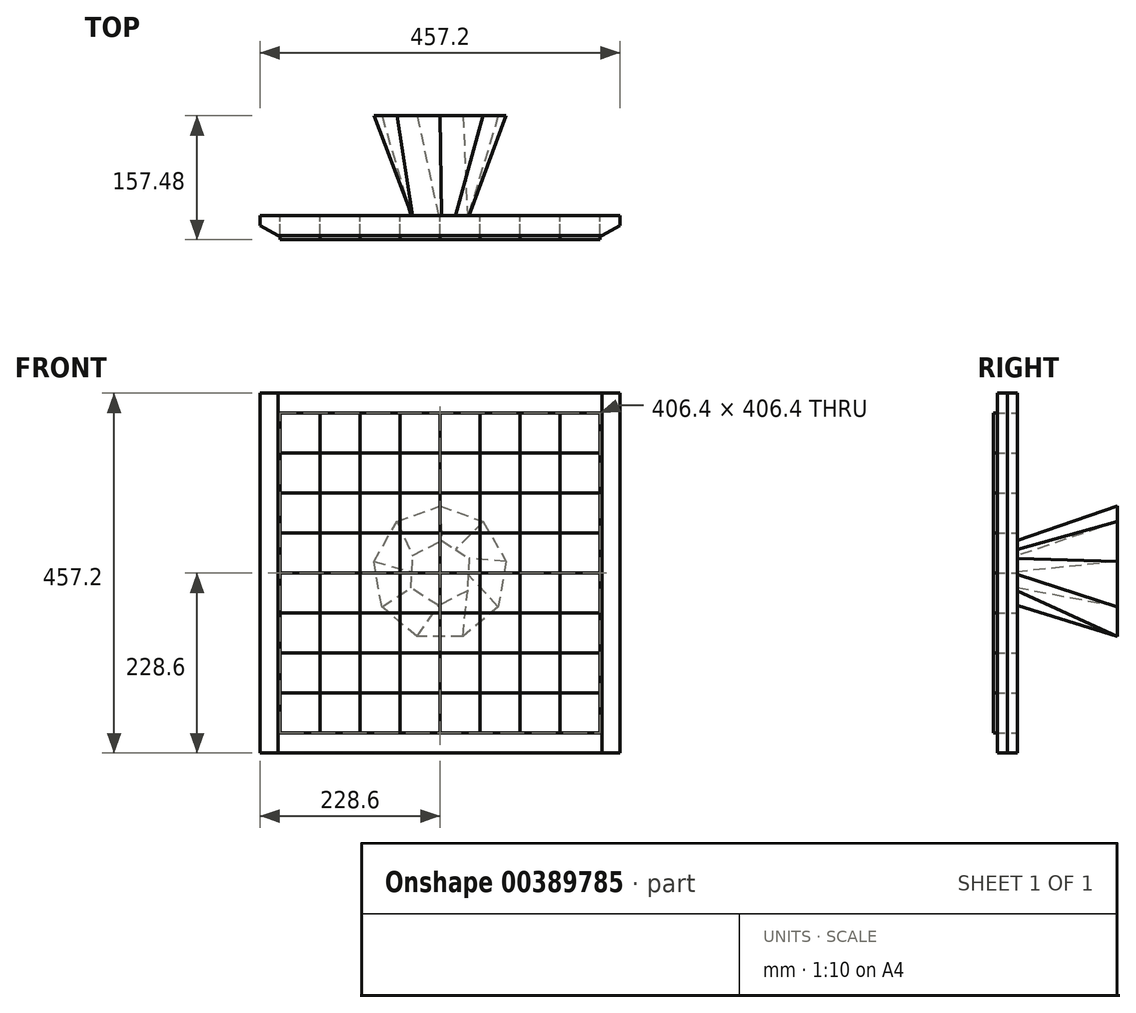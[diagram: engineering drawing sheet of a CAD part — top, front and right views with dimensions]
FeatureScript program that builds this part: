
annotation { "Feature Type Name" : "Feature", "Feature Type Description" : "" }
export const myFeature = defineFeature(function(context is Context, id is Id, definition is map)
    precondition{}
    {
        {
            var Q0;
            Q0=qCreatedBy(makeId("Front.planeOp"),FACE);
            var sketch = newSketch(context, id + "F0", { "sketchPlane" : qUnion([Q0])});
            skLineSegment(sketch, "E0.left", {"start": v(-203.2, 203.2) * mm, "end": v(-203.2, 0) * mm});
            skLineSegment(sketch, "E0.right", {"start": v(203.2, 203.2) * mm, "end": v(203.2, 0) * mm});
            skPoint(sketch, "E0.middle", {"position": v(0, 0) * mm});
            skLineSegment(sketch, "E1", {"start": v(-203.2, 203.2) * mm, "end": v(0, 203.2) * mm});
            skLineSegment(sketch, "E2", {"start": v(0, -203.2) * mm, "end": v(-203.2, -203.2) * mm});
            skLineSegment(sketch, "E3", {"start": v(0, 203.2) * mm, "end": v(0, -203.2) * mm});
            skLineSegment(sketch, "E4", {"start": v(101.6, 203.2) * mm, "end": v(101.6, -203.2) * mm});
            skLineSegment(sketch, "E5", {"start": v(203.2, -203.2) * mm, "end": v(101.6, -203.2) * mm});
            skLineSegment(sketch, "E6", {"start": v(101.6, -203.2) * mm, "end": v(0, -203.2) * mm});
            skLineSegment(sketch, "E7", {"start": v(203.2, 203.2) * mm, "end": v(101.6, 203.2) * mm});
            skLineSegment(sketch, "E8", {"start": v(101.6, 203.2) * mm, "end": v(0, 203.2) * mm});
            skLineSegment(sketch, "E9", {"start": v(50.8, 203.2) * mm, "end": v(50.8, -203.2) * mm});
            skLineSegment(sketch, "E10", {"start": v(152.4, -203.2) * mm, "end": v(152.4, 203.2) * mm});
            skLineSegment(sketch, "E11.MirrorCS", {"start": v(-152.4, -203.2) * mm, "end": v(-152.4, 203.2) * mm});
            skLineSegment(sketch, "E12.MirrorCS", {"start": v(-50.8, 203.2) * mm, "end": v(-50.8, -203.2) * mm});
            skLineSegment(sketch, "E13.MirrorCS", {"start": v(-101.6, 203.2) * mm, "end": v(-101.6, -203.2) * mm});
            skLineSegment(sketch, "E14", {"start": v(203.2, 0) * mm, "end": v(-203.2, 0) * mm});
            skLineSegment(sketch, "E15", {"start": v(203.2, -101.6) * mm, "end": v(-203.2, -101.6) * mm});
            skLineSegment(sketch, "E16", {"start": v(203.2, -203.2) * mm, "end": v(203.2, -101.6) * mm});
            skLineSegment(sketch, "E17", {"start": v(203.2, -101.6) * mm, "end": v(203.2, 0) * mm});
            skLineSegment(sketch, "E18", {"start": v(-203.2, -203.2) * mm, "end": v(-203.2, -101.6) * mm});
            skLineSegment(sketch, "E19", {"start": v(-203.2, -101.6) * mm, "end": v(-203.2, 0) * mm});
            skLineSegment(sketch, "E20", {"start": v(-203.2, -50.8) * mm, "end": v(203.2, -50.8) * mm});
            skLineSegment(sketch, "E21", {"start": v(-203.2, -152.4) * mm, "end": v(203.2, -152.4) * mm});
            skLineSegment(sketch, "E22.MirrorCS", {"start": v(-203.2, 50.8) * mm, "end": v(203.2, 50.8) * mm});
            skLineSegment(sketch, "E23.MirrorCS", {"start": v(203.2, 101.6) * mm, "end": v(-203.2, 101.6) * mm});
            skLineSegment(sketch, "E24.MirrorCS", {"start": v(-203.2, 152.4) * mm, "end": v(203.2, 152.4) * mm});
            skLineSegment(sketch, "E25.0", {"start": v(-228.6, 228.6) * mm, "end": v(-228.6, 0) * mm});
            skLineSegment(sketch, "E25.1", {"start": v(228.6, -101.6) * mm, "end": v(228.6, 0) * mm});
            skLineSegment(sketch, "E25.2", {"start": v(228.6, 228.6) * mm, "end": v(228.6, 0) * mm});
            skLineSegment(sketch, "E25.3", {"start": v(228.6, 228.6) * mm, "end": v(101.6, 228.6) * mm});
            skLineSegment(sketch, "E25.4", {"start": v(101.6, 228.6) * mm, "end": v(0, 228.6) * mm});
            skLineSegment(sketch, "E25.5", {"start": v(228.6, -228.6) * mm, "end": v(228.6, -101.6) * mm});
            skLineSegment(sketch, "E25.6", {"start": v(-228.6, 228.6) * mm, "end": v(0, 228.6) * mm});
            skLineSegment(sketch, "E25.7", {"start": v(228.6, -228.6) * mm, "end": v(101.6, -228.6) * mm});
            skLineSegment(sketch, "E25.8", {"start": v(101.6, -228.6) * mm, "end": v(0, -228.6) * mm});
            skLineSegment(sketch, "E25.9", {"start": v(0, -228.6) * mm, "end": v(-228.6, -228.6) * mm});
            skLineSegment(sketch, "E25.10", {"start": v(-228.6, -228.6) * mm, "end": v(-228.6, -101.6) * mm});
            skLineSegment(sketch, "E25.11", {"start": v(-228.6, -101.6) * mm, "end": v(-228.6, 0) * mm});
            skSolve(sketch);
        }
        {
            var Q0;
            Q0=makeQuery(id+"F0.imprint","IMPRINT",FACE,{"disambiguationData":[TD([[makeQuery(id+"F0.imprint","IMPRINT",EDGE,{"derivedFrom":sQuery(id+"F0.wireOp",EDGE,"E25.0")}),1.0]])]});
            extrude(context, id + "F1", {"entities" : qUnion([Q0]), "depth" : 25.4 * mm});
        }
        {
            var Q0;
            {var subQ0=sQuery(id+"F0.wireOp",EDGE,"E1");var subQ1=sQuery(id+"F0.wireOp",EDGE,"E0.left");var subQ2=makeQuery(id+"F0.imprint","INTERSECT",VERTEX,{"derivedFrom":[subQ1,subQ0]});Q0=makeQuery(id+"F0.imprint","IMPRINT",FACE,{"disambiguationData":[TD([[makeQuery(id+"F0.imprint","IMPRINT",EDGE,{"disambiguationData":[TD([[subQ2,-1.0]])],"derivedFrom":subQ1}),1.0]])]});}
            var Q1;
            {var subQ0=sQuery(id+"F0.wireOp",EDGE,"E13.MirrorCS");var subQ1=sQuery(id+"F0.wireOp",EDGE,"E1");var subQ2=makeQuery(id+"F0.imprint","INTERSECT",VERTEX,{"derivedFrom":[subQ1,subQ0]});Q1=makeQuery(id+"F0.imprint","IMPRINT",FACE,{"disambiguationData":[TD([[makeQuery(id+"F0.imprint","IMPRINT",EDGE,{"disambiguationData":[TD([[subQ2,-1.0]])],"derivedFrom":subQ1}),-1.0]])]});}
            var Q2;
            {var subQ0=sQuery(id+"F0.wireOp",EDGE,"E8");var subQ5=sQuery(id+"F0.wireOp",EDGE,"E9");var subQ6=makeQuery(id+"F0.imprint","INTERSECT",VERTEX,{"derivedFrom":[subQ0,subQ5]});Q2=makeQuery(id+"F0.imprint","IMPRINT",FACE,{"disambiguationData":[TD([[makeQuery(id+"F0.imprint","IMPRINT",EDGE,{"disambiguationData":[TD([[subQ6,-1.0]])],"derivedFrom":subQ5}),-1.0]])]});}
            var Q3;
            {var subQ0=sQuery(id+"F0.wireOp",EDGE,"E7");var subQ5=sQuery(id+"F0.wireOp",EDGE,"E10");var subQ6=makeQuery(id+"F0.imprint","INTERSECT",VERTEX,{"derivedFrom":[subQ0,subQ5]});Q3=makeQuery(id+"F0.imprint","IMPRINT",FACE,{"disambiguationData":[TD([[makeQuery(id+"F0.imprint","IMPRINT",EDGE,{"disambiguationData":[TD([[subQ6,1.0]])],"derivedFrom":subQ5}),1.0]])]});}
            var Q4;
            {var subQ0=sQuery(id+"F0.wireOp",EDGE,"E23.MirrorCS");var subQ1=sQuery(id+"F0.wireOp",EDGE,"E0.right");var subQ2=makeQuery(id+"F0.imprint","INTERSECT",VERTEX,{"derivedFrom":[subQ1,subQ0]});Q4=makeQuery(id+"F0.imprint","IMPRINT",FACE,{"disambiguationData":[TD([[makeQuery(id+"F0.imprint","IMPRINT",EDGE,{"disambiguationData":[TD([[subQ2,1.0]])],"derivedFrom":subQ1}),-1.0]])]});}
            var Q5;
            {var subQ0=sQuery(id+"F0.wireOp",EDGE,"E24.MirrorCS");var subQ1=sQuery(id+"F0.wireOp",EDGE,"E4");var subQ2=makeQuery(id+"F0.imprint","INTERSECT",VERTEX,{"derivedFrom":[subQ1,subQ0]});Q5=makeQuery(id+"F0.imprint","IMPRINT",FACE,{"disambiguationData":[TD([[makeQuery(id+"F0.imprint","IMPRINT",EDGE,{"disambiguationData":[TD([[subQ2,-1.0]])],"derivedFrom":subQ1}),-1.0]])]});}
            var Q6;
            {var subQ0=sQuery(id+"F0.wireOp",EDGE,"E24.MirrorCS");var subQ1=sQuery(id+"F0.wireOp",EDGE,"E3");var subQ2=makeQuery(id+"F0.imprint","INTERSECT",VERTEX,{"derivedFrom":[subQ1,subQ0]});Q6=makeQuery(id+"F0.imprint","IMPRINT",FACE,{"disambiguationData":[TD([[makeQuery(id+"F0.imprint","IMPRINT",EDGE,{"disambiguationData":[TD([[subQ2,-1.0]])],"derivedFrom":subQ1}),-1.0]])]});}
            var Q7;
            {var subQ0=sQuery(id+"F0.wireOp",EDGE,"E23.MirrorCS");var subQ1=sQuery(id+"F0.wireOp",EDGE,"E11.MirrorCS");var subQ2=makeQuery(id+"F0.imprint","INTERSECT",VERTEX,{"derivedFrom":[subQ1,subQ0]});Q7=makeQuery(id+"F0.imprint","IMPRINT",FACE,{"disambiguationData":[TD([[makeQuery(id+"F0.imprint","IMPRINT",EDGE,{"disambiguationData":[TD([[subQ2,-1.0]])],"derivedFrom":subQ1}),-1.0]])]});}
            var Q8;
            {var subQ0=sQuery(id+"F0.wireOp",EDGE,"E22.MirrorCS");var subQ1=sQuery(id+"F0.wireOp",EDGE,"E0.left");var subQ2=makeQuery(id+"F0.imprint","INTERSECT",VERTEX,{"derivedFrom":[subQ1,subQ0]});Q8=makeQuery(id+"F0.imprint","IMPRINT",FACE,{"disambiguationData":[TD([[makeQuery(id+"F0.imprint","IMPRINT",EDGE,{"disambiguationData":[TD([[subQ2,1.0]])],"derivedFrom":subQ1}),1.0]])]});}
            var Q9;
            {var subQ0=sQuery(id+"F0.wireOp",EDGE,"E23.MirrorCS");var subQ1=sQuery(id+"F0.wireOp",EDGE,"E13.MirrorCS");var subQ2=makeQuery(id+"F0.imprint","INTERSECT",VERTEX,{"derivedFrom":[subQ1,subQ0]});Q9=makeQuery(id+"F0.imprint","IMPRINT",FACE,{"disambiguationData":[TD([[makeQuery(id+"F0.imprint","IMPRINT",EDGE,{"disambiguationData":[TD([[subQ2,-1.0]])],"derivedFrom":subQ1}),1.0]])]});}
            var Q10;
            {var subQ0=sQuery(id+"F0.wireOp",EDGE,"E23.MirrorCS");var subQ1=sQuery(id+"F0.wireOp",EDGE,"E3");var subQ2=makeQuery(id+"F0.imprint","INTERSECT",VERTEX,{"derivedFrom":[subQ1,subQ0]});Q10=makeQuery(id+"F0.imprint","IMPRINT",FACE,{"disambiguationData":[TD([[makeQuery(id+"F0.imprint","IMPRINT",EDGE,{"disambiguationData":[TD([[subQ2,-1.0]])],"derivedFrom":subQ1}),1.0]])]});}
            var Q11;
            {var subQ0=sQuery(id+"F0.wireOp",EDGE,"E23.MirrorCS");var subQ1=sQuery(id+"F0.wireOp",EDGE,"E4");var subQ2=makeQuery(id+"F0.imprint","INTERSECT",VERTEX,{"derivedFrom":[subQ1,subQ0]});Q11=makeQuery(id+"F0.imprint","IMPRINT",FACE,{"disambiguationData":[TD([[makeQuery(id+"F0.imprint","IMPRINT",EDGE,{"disambiguationData":[TD([[subQ2,-1.0]])],"derivedFrom":subQ1}),1.0]])]});}
            var Q12;
            {var subQ0=sQuery(id+"F0.wireOp",EDGE,"E14");var subQ5=sQuery(id+"F0.wireOp",EDGE,"E10");var subQ6=makeQuery(id+"F0.imprint","INTERSECT",VERTEX,{"derivedFrom":[subQ5,subQ0]});Q12=makeQuery(id+"F0.imprint","IMPRINT",FACE,{"disambiguationData":[TD([[makeQuery(id+"F0.imprint","IMPRINT",EDGE,{"disambiguationData":[TD([[subQ6,-1.0]])],"derivedFrom":subQ5}),-1.0]])]});}
            var Q13;
            {var subQ0=sQuery(id+"F0.wireOp",EDGE,"E22.MirrorCS");var subQ1=sQuery(id+"F0.wireOp",EDGE,"E4");var subQ2=makeQuery(id+"F0.imprint","INTERSECT",VERTEX,{"derivedFrom":[subQ1,subQ0]});Q13=makeQuery(id+"F0.imprint","IMPRINT",FACE,{"disambiguationData":[TD([[makeQuery(id+"F0.imprint","IMPRINT",EDGE,{"disambiguationData":[TD([[subQ2,-1.0]])],"derivedFrom":subQ1}),-1.0]])]});}
            var Q14;
            {var subQ0=sQuery(id+"F0.wireOp",EDGE,"E22.MirrorCS");var subQ1=sQuery(id+"F0.wireOp",EDGE,"E3");var subQ2=makeQuery(id+"F0.imprint","INTERSECT",VERTEX,{"derivedFrom":[subQ1,subQ0]});Q14=makeQuery(id+"F0.imprint","IMPRINT",FACE,{"disambiguationData":[TD([[makeQuery(id+"F0.imprint","IMPRINT",EDGE,{"disambiguationData":[TD([[subQ2,-1.0]])],"derivedFrom":subQ1}),-1.0]])]});}
            var Q15;
            {var subQ0=sQuery(id+"F0.wireOp",EDGE,"E14");var subQ1=sQuery(id+"F0.wireOp",EDGE,"E11.MirrorCS");var subQ2=makeQuery(id+"F0.imprint","INTERSECT",VERTEX,{"derivedFrom":[subQ1,subQ0]});Q15=makeQuery(id+"F0.imprint","IMPRINT",FACE,{"disambiguationData":[TD([[makeQuery(id+"F0.imprint","IMPRINT",EDGE,{"disambiguationData":[TD([[subQ2,-1.0]])],"derivedFrom":subQ1}),-1.0]])]});}
            var Q16;
            {var subQ0=sQuery(id+"F0.wireOp",EDGE,"E20");var subQ1=sQuery(id+"F0.wireOp",EDGE,"E11.MirrorCS");var subQ2=makeQuery(id+"F0.imprint","INTERSECT",VERTEX,{"derivedFrom":[subQ1,subQ0]});Q16=makeQuery(id+"F0.imprint","IMPRINT",FACE,{"disambiguationData":[TD([[makeQuery(id+"F0.imprint","IMPRINT",EDGE,{"disambiguationData":[TD([[subQ2,-1.0]])],"derivedFrom":subQ1}),1.0]])]});}
            var Q17;
            {var subQ0=sQuery(id+"F0.wireOp",EDGE,"E14");var subQ1=sQuery(id+"F0.wireOp",EDGE,"E13.MirrorCS");var subQ2=makeQuery(id+"F0.imprint","INTERSECT",VERTEX,{"derivedFrom":[subQ1,subQ0]});Q17=makeQuery(id+"F0.imprint","IMPRINT",FACE,{"disambiguationData":[TD([[makeQuery(id+"F0.imprint","IMPRINT",EDGE,{"disambiguationData":[TD([[subQ2,-1.0]])],"derivedFrom":subQ1}),1.0]])]});}
            var Q18;
            {var subQ0=sQuery(id+"F0.wireOp",EDGE,"E14");var subQ1=sQuery(id+"F0.wireOp",EDGE,"E3");var subQ2=makeQuery(id+"F0.imprint","INTERSECT",VERTEX,{"derivedFrom":[subQ1,subQ0]});Q18=makeQuery(id+"F0.imprint","IMPRINT",FACE,{"disambiguationData":[TD([[makeQuery(id+"F0.imprint","IMPRINT",EDGE,{"disambiguationData":[TD([[subQ2,-1.0]])],"derivedFrom":subQ1}),1.0]])]});}
            var Q19;
            {var subQ0=sQuery(id+"F0.wireOp",EDGE,"E14");var subQ1=sQuery(id+"F0.wireOp",EDGE,"E4");var subQ2=makeQuery(id+"F0.imprint","INTERSECT",VERTEX,{"derivedFrom":[subQ1,subQ0]});Q19=makeQuery(id+"F0.imprint","IMPRINT",FACE,{"disambiguationData":[TD([[makeQuery(id+"F0.imprint","IMPRINT",EDGE,{"disambiguationData":[TD([[subQ2,-1.0]])],"derivedFrom":subQ1}),1.0]])]});}
            var Q20;
            {var subQ0=sQuery(id+"F0.wireOp",EDGE,"E15");var subQ1=sQuery(id+"F0.wireOp",EDGE,"E10");var subQ2=makeQuery(id+"F0.imprint","INTERSECT",VERTEX,{"derivedFrom":[subQ1,subQ0]});Q20=makeQuery(id+"F0.imprint","IMPRINT",FACE,{"disambiguationData":[TD([[makeQuery(id+"F0.imprint","IMPRINT",EDGE,{"disambiguationData":[TD([[subQ2,-1.0]])],"derivedFrom":subQ1}),-1.0]])]});}
            var Q21;
            {var subQ0=sQuery(id+"F0.wireOp",EDGE,"E20");var subQ1=sQuery(id+"F0.wireOp",EDGE,"E4");var subQ2=makeQuery(id+"F0.imprint","INTERSECT",VERTEX,{"derivedFrom":[subQ1,subQ0]});Q21=makeQuery(id+"F0.imprint","IMPRINT",FACE,{"disambiguationData":[TD([[makeQuery(id+"F0.imprint","IMPRINT",EDGE,{"disambiguationData":[TD([[subQ2,-1.0]])],"derivedFrom":subQ1}),-1.0]])]});}
            var Q22;
            {var subQ0=sQuery(id+"F0.wireOp",EDGE,"E20");var subQ1=sQuery(id+"F0.wireOp",EDGE,"E3");var subQ2=makeQuery(id+"F0.imprint","INTERSECT",VERTEX,{"derivedFrom":[subQ1,subQ0]});Q22=makeQuery(id+"F0.imprint","IMPRINT",FACE,{"disambiguationData":[TD([[makeQuery(id+"F0.imprint","IMPRINT",EDGE,{"disambiguationData":[TD([[subQ2,-1.0]])],"derivedFrom":subQ1}),-1.0]])]});}
            var Q23;
            {var subQ0=sQuery(id+"F0.wireOp",EDGE,"E15");var subQ1=sQuery(id+"F0.wireOp",EDGE,"E11.MirrorCS");var subQ2=makeQuery(id+"F0.imprint","INTERSECT",VERTEX,{"derivedFrom":[subQ1,subQ0]});Q23=makeQuery(id+"F0.imprint","IMPRINT",FACE,{"disambiguationData":[TD([[makeQuery(id+"F0.imprint","IMPRINT",EDGE,{"disambiguationData":[TD([[subQ2,-1.0]])],"derivedFrom":subQ1}),-1.0]])]});}
            var Q24;
            {var subQ0=sQuery(id+"F0.wireOp",EDGE,"E21");var subQ1=sQuery(id+"F0.wireOp",EDGE,"E11.MirrorCS");var subQ2=makeQuery(id+"F0.imprint","INTERSECT",VERTEX,{"derivedFrom":[subQ1,subQ0]});Q24=makeQuery(id+"F0.imprint","IMPRINT",FACE,{"disambiguationData":[TD([[makeQuery(id+"F0.imprint","IMPRINT",EDGE,{"disambiguationData":[TD([[subQ2,-1.0]])],"derivedFrom":subQ1}),1.0]])]});}
            var Q25;
            {var subQ0=sQuery(id+"F0.wireOp",EDGE,"E15");var subQ1=sQuery(id+"F0.wireOp",EDGE,"E13.MirrorCS");var subQ2=makeQuery(id+"F0.imprint","INTERSECT",VERTEX,{"derivedFrom":[subQ1,subQ0]});Q25=makeQuery(id+"F0.imprint","IMPRINT",FACE,{"disambiguationData":[TD([[makeQuery(id+"F0.imprint","IMPRINT",EDGE,{"disambiguationData":[TD([[subQ2,-1.0]])],"derivedFrom":subQ1}),1.0]])]});}
            var Q26;
            {var subQ0=sQuery(id+"F0.wireOp",EDGE,"E15");var subQ1=sQuery(id+"F0.wireOp",EDGE,"E3");var subQ2=makeQuery(id+"F0.imprint","INTERSECT",VERTEX,{"derivedFrom":[subQ1,subQ0]});Q26=makeQuery(id+"F0.imprint","IMPRINT",FACE,{"disambiguationData":[TD([[makeQuery(id+"F0.imprint","IMPRINT",EDGE,{"disambiguationData":[TD([[subQ2,-1.0]])],"derivedFrom":subQ1}),1.0]])]});}
            var Q27;
            {var subQ0=sQuery(id+"F0.wireOp",EDGE,"E15");var subQ1=sQuery(id+"F0.wireOp",EDGE,"E4");var subQ2=makeQuery(id+"F0.imprint","INTERSECT",VERTEX,{"derivedFrom":[subQ1,subQ0]});Q27=makeQuery(id+"F0.imprint","IMPRINT",FACE,{"disambiguationData":[TD([[makeQuery(id+"F0.imprint","IMPRINT",EDGE,{"disambiguationData":[TD([[subQ2,-1.0]])],"derivedFrom":subQ1}),1.0]])]});}
            var Q28;
            {var subQ0=sQuery(id+"F0.wireOp",EDGE,"E16");var subQ1=sQuery(id+"F0.wireOp",EDGE,"E5");var subQ2=makeQuery(id+"F0.imprint","INTERSECT",VERTEX,{"derivedFrom":[subQ1,subQ0]});Q28=makeQuery(id+"F0.imprint","IMPRINT",FACE,{"disambiguationData":[TD([[makeQuery(id+"F0.imprint","IMPRINT",EDGE,{"disambiguationData":[TD([[subQ2,-1.0]])],"derivedFrom":subQ1}),-1.0]])]});}
            var Q29;
            {var subQ0=sQuery(id+"F0.wireOp",EDGE,"E6");var subQ5=sQuery(id+"F0.wireOp",EDGE,"E9");var subQ6=makeQuery(id+"F0.imprint","INTERSECT",VERTEX,{"derivedFrom":[subQ0,subQ5]});Q29=makeQuery(id+"F0.imprint","IMPRINT",FACE,{"disambiguationData":[TD([[makeQuery(id+"F0.imprint","IMPRINT",EDGE,{"disambiguationData":[TD([[subQ6,1.0]])],"derivedFrom":subQ5}),1.0]])]});}
            var Q30;
            {var subQ1=sQuery(id+"F0.wireOp",EDGE,"E2");var subQ3=sQuery(id+"F0.wireOp",EDGE,"E12.MirrorCS");var subQ4=makeQuery(id+"F0.imprint","INTERSECT",VERTEX,{"derivedFrom":[subQ1,subQ3]});Q30=makeQuery(id+"F0.imprint","IMPRINT",FACE,{"disambiguationData":[TD([[makeQuery(id+"F0.imprint","IMPRINT",EDGE,{"disambiguationData":[TD([[subQ4,1.0]])],"derivedFrom":subQ3}),1.0]])]});}
            var Q31;
            {var subQ0=sQuery(id+"F0.wireOp",EDGE,"E11.MirrorCS");var subQ1=sQuery(id+"F0.wireOp",EDGE,"E2");var subQ2=makeQuery(id+"F0.imprint","INTERSECT",VERTEX,{"derivedFrom":[subQ1,subQ0]});Q31=makeQuery(id+"F0.imprint","IMPRINT",FACE,{"disambiguationData":[TD([[makeQuery(id+"F0.imprint","IMPRINT",EDGE,{"disambiguationData":[TD([[subQ2,1.0]])],"derivedFrom":subQ1}),-1.0]])]});}
            extrude(context, id + "F2", {"entities" : qUnion([Q0, Q1, Q2, Q3, Q4, Q5, Q6, Q7, Q8, Q9, Q10, Q11, Q12, Q13, Q14, Q15, Q16, Q17, Q18, Q19, Q20, Q21, Q22, Q23, Q24, Q25, Q26, Q27, Q28, Q29, Q30, Q31]), "depth" : 30.48 * mm});
        }
        {
            var Q0;
            {var subQ0=sQuery(id+"F0.wireOp",EDGE,"E11.MirrorCS");var subQ1=sQuery(id+"F0.wireOp",EDGE,"E1");var subQ2=makeQuery(id+"F0.imprint","INTERSECT",VERTEX,{"derivedFrom":[subQ1,subQ0]});Q0=makeQuery(id+"F0.imprint","IMPRINT",FACE,{"disambiguationData":[TD([[makeQuery(id+"F0.imprint","IMPRINT",EDGE,{"disambiguationData":[TD([[subQ2,-1.0]])],"derivedFrom":subQ1}),-1.0]])]});}
            var Q1;
            {var subQ1=sQuery(id+"F0.wireOp",EDGE,"E1");var subQ3=sQuery(id+"F0.wireOp",EDGE,"E12.MirrorCS");var subQ4=makeQuery(id+"F0.imprint","INTERSECT",VERTEX,{"derivedFrom":[subQ1,subQ3]});Q1=makeQuery(id+"F0.imprint","IMPRINT",FACE,{"disambiguationData":[TD([[makeQuery(id+"F0.imprint","IMPRINT",EDGE,{"disambiguationData":[TD([[subQ4,-1.0]])],"derivedFrom":subQ3}),1.0]])]});}
            var Q2;
            {var subQ0=sQuery(id+"F0.wireOp",EDGE,"E8");var subQ5=sQuery(id+"F0.wireOp",EDGE,"E9");var subQ6=makeQuery(id+"F0.imprint","INTERSECT",VERTEX,{"derivedFrom":[subQ0,subQ5]});Q2=makeQuery(id+"F0.imprint","IMPRINT",FACE,{"disambiguationData":[TD([[makeQuery(id+"F0.imprint","IMPRINT",EDGE,{"disambiguationData":[TD([[subQ6,-1.0]])],"derivedFrom":subQ5}),1.0]])]});}
            var Q3;
            {var subQ0=sQuery(id+"F0.wireOp",EDGE,"E7");var subQ1=sQuery(id+"F0.wireOp",EDGE,"E0.right");var subQ2=makeQuery(id+"F0.imprint","INTERSECT",VERTEX,{"derivedFrom":[subQ1,subQ0]});Q3=makeQuery(id+"F0.imprint","IMPRINT",FACE,{"disambiguationData":[TD([[makeQuery(id+"F0.imprint","IMPRINT",EDGE,{"disambiguationData":[TD([[subQ2,-1.0]])],"derivedFrom":subQ1}),-1.0]])]});}
            var Q4;
            {var subQ0=sQuery(id+"F0.wireOp",EDGE,"E24.MirrorCS");var subQ1=sQuery(id+"F0.wireOp",EDGE,"E4");var subQ2=makeQuery(id+"F0.imprint","INTERSECT",VERTEX,{"derivedFrom":[subQ1,subQ0]});Q4=makeQuery(id+"F0.imprint","IMPRINT",FACE,{"disambiguationData":[TD([[makeQuery(id+"F0.imprint","IMPRINT",EDGE,{"disambiguationData":[TD([[subQ2,-1.0]])],"derivedFrom":subQ1}),1.0]])]});}
            var Q5;
            {var subQ0=sQuery(id+"F0.wireOp",EDGE,"E22.MirrorCS");var subQ1=sQuery(id+"F0.wireOp",EDGE,"E0.right");var subQ2=makeQuery(id+"F0.imprint","INTERSECT",VERTEX,{"derivedFrom":[subQ1,subQ0]});Q5=makeQuery(id+"F0.imprint","IMPRINT",FACE,{"disambiguationData":[TD([[makeQuery(id+"F0.imprint","IMPRINT",EDGE,{"disambiguationData":[TD([[subQ2,1.0]])],"derivedFrom":subQ1}),-1.0]])]});}
            var Q6;
            {var subQ0=sQuery(id+"F0.wireOp",EDGE,"E22.MirrorCS");var subQ1=sQuery(id+"F0.wireOp",EDGE,"E4");var subQ2=makeQuery(id+"F0.imprint","INTERSECT",VERTEX,{"derivedFrom":[subQ1,subQ0]});Q6=makeQuery(id+"F0.imprint","IMPRINT",FACE,{"disambiguationData":[TD([[makeQuery(id+"F0.imprint","IMPRINT",EDGE,{"disambiguationData":[TD([[subQ2,-1.0]])],"derivedFrom":subQ1}),1.0]])]});}
            var Q7;
            {var subQ0=sQuery(id+"F0.wireOp",EDGE,"E20");var subQ1=sQuery(id+"F0.wireOp",EDGE,"E10");var subQ2=makeQuery(id+"F0.imprint","INTERSECT",VERTEX,{"derivedFrom":[subQ1,subQ0]});Q7=makeQuery(id+"F0.imprint","IMPRINT",FACE,{"disambiguationData":[TD([[makeQuery(id+"F0.imprint","IMPRINT",EDGE,{"disambiguationData":[TD([[subQ2,-1.0]])],"derivedFrom":subQ1}),-1.0]])]});}
            var Q8;
            {var subQ0=sQuery(id+"F0.wireOp",EDGE,"E20");var subQ1=sQuery(id+"F0.wireOp",EDGE,"E4");var subQ2=makeQuery(id+"F0.imprint","INTERSECT",VERTEX,{"derivedFrom":[subQ1,subQ0]});Q8=makeQuery(id+"F0.imprint","IMPRINT",FACE,{"disambiguationData":[TD([[makeQuery(id+"F0.imprint","IMPRINT",EDGE,{"disambiguationData":[TD([[subQ2,-1.0]])],"derivedFrom":subQ1}),1.0]])]});}
            var Q9;
            {var subQ0=sQuery(id+"F0.wireOp",EDGE,"E21");var subQ1=sQuery(id+"F0.wireOp",EDGE,"E10");var subQ2=makeQuery(id+"F0.imprint","INTERSECT",VERTEX,{"derivedFrom":[subQ1,subQ0]});Q9=makeQuery(id+"F0.imprint","IMPRINT",FACE,{"disambiguationData":[TD([[makeQuery(id+"F0.imprint","IMPRINT",EDGE,{"disambiguationData":[TD([[subQ2,-1.0]])],"derivedFrom":subQ1}),-1.0]])]});}
            var Q10;
            {var subQ0=sQuery(id+"F0.wireOp",EDGE,"E5");var subQ5=sQuery(id+"F0.wireOp",EDGE,"E10");var subQ6=makeQuery(id+"F0.imprint","INTERSECT",VERTEX,{"derivedFrom":[subQ0,subQ5]});Q10=makeQuery(id+"F0.imprint","IMPRINT",FACE,{"disambiguationData":[TD([[makeQuery(id+"F0.imprint","IMPRINT",EDGE,{"disambiguationData":[TD([[subQ6,-1.0]])],"derivedFrom":subQ5}),1.0]])]});}
            var Q11;
            {var subQ0=sQuery(id+"F0.wireOp",EDGE,"E15");var subQ1=sQuery(id+"F0.wireOp",EDGE,"E4");var subQ2=makeQuery(id+"F0.imprint","INTERSECT",VERTEX,{"derivedFrom":[subQ1,subQ0]});Q11=makeQuery(id+"F0.imprint","IMPRINT",FACE,{"disambiguationData":[TD([[makeQuery(id+"F0.imprint","IMPRINT",EDGE,{"disambiguationData":[TD([[subQ2,-1.0]])],"derivedFrom":subQ1}),-1.0]])]});}
            var Q12;
            {var subQ0=sQuery(id+"F0.wireOp",EDGE,"E6");var subQ5=sQuery(id+"F0.wireOp",EDGE,"E9");var subQ6=makeQuery(id+"F0.imprint","INTERSECT",VERTEX,{"derivedFrom":[subQ0,subQ5]});Q12=makeQuery(id+"F0.imprint","IMPRINT",FACE,{"disambiguationData":[TD([[makeQuery(id+"F0.imprint","IMPRINT",EDGE,{"disambiguationData":[TD([[subQ6,1.0]])],"derivedFrom":subQ5}),-1.0]])]});}
            var Q13;
            {var subQ0=sQuery(id+"F0.wireOp",EDGE,"E15");var subQ1=sQuery(id+"F0.wireOp",EDGE,"E3");var subQ2=makeQuery(id+"F0.imprint","INTERSECT",VERTEX,{"derivedFrom":[subQ1,subQ0]});Q13=makeQuery(id+"F0.imprint","IMPRINT",FACE,{"disambiguationData":[TD([[makeQuery(id+"F0.imprint","IMPRINT",EDGE,{"disambiguationData":[TD([[subQ2,-1.0]])],"derivedFrom":subQ1}),-1.0]])]});}
            var Q14;
            {var subQ0=sQuery(id+"F0.wireOp",EDGE,"E13.MirrorCS");var subQ1=sQuery(id+"F0.wireOp",EDGE,"E2");var subQ2=makeQuery(id+"F0.imprint","INTERSECT",VERTEX,{"derivedFrom":[subQ1,subQ0]});Q14=makeQuery(id+"F0.imprint","IMPRINT",FACE,{"disambiguationData":[TD([[makeQuery(id+"F0.imprint","IMPRINT",EDGE,{"disambiguationData":[TD([[subQ2,1.0]])],"derivedFrom":subQ1}),-1.0]])]});}
            var Q15;
            {var subQ0=sQuery(id+"F0.wireOp",EDGE,"E18");var subQ1=sQuery(id+"F0.wireOp",EDGE,"E2");var subQ2=makeQuery(id+"F0.imprint","INTERSECT",VERTEX,{"derivedFrom":[subQ1,subQ0]});Q15=makeQuery(id+"F0.imprint","IMPRINT",FACE,{"disambiguationData":[TD([[makeQuery(id+"F0.imprint","IMPRINT",EDGE,{"disambiguationData":[TD([[subQ2,1.0]])],"derivedFrom":subQ1}),-1.0]])]});}
            var Q16;
            {var subQ0=sQuery(id+"F0.wireOp",EDGE,"E21");var subQ1=sQuery(id+"F0.wireOp",EDGE,"E11.MirrorCS");var subQ2=makeQuery(id+"F0.imprint","INTERSECT",VERTEX,{"derivedFrom":[subQ1,subQ0]});Q16=makeQuery(id+"F0.imprint","IMPRINT",FACE,{"disambiguationData":[TD([[makeQuery(id+"F0.imprint","IMPRINT",EDGE,{"disambiguationData":[TD([[subQ2,-1.0]])],"derivedFrom":subQ1}),-1.0]])]});}
            var Q17;
            {var subQ0=sQuery(id+"F0.wireOp",EDGE,"E15");var subQ1=sQuery(id+"F0.wireOp",EDGE,"E11.MirrorCS");var subQ2=makeQuery(id+"F0.imprint","INTERSECT",VERTEX,{"derivedFrom":[subQ1,subQ0]});Q17=makeQuery(id+"F0.imprint","IMPRINT",FACE,{"disambiguationData":[TD([[makeQuery(id+"F0.imprint","IMPRINT",EDGE,{"disambiguationData":[TD([[subQ2,-1.0]])],"derivedFrom":subQ1}),1.0]])]});}
            var Q18;
            {var subQ0=sQuery(id+"F0.wireOp",EDGE,"E20");var subQ1=sQuery(id+"F0.wireOp",EDGE,"E11.MirrorCS");var subQ2=makeQuery(id+"F0.imprint","INTERSECT",VERTEX,{"derivedFrom":[subQ1,subQ0]});Q18=makeQuery(id+"F0.imprint","IMPRINT",FACE,{"disambiguationData":[TD([[makeQuery(id+"F0.imprint","IMPRINT",EDGE,{"disambiguationData":[TD([[subQ2,-1.0]])],"derivedFrom":subQ1}),-1.0]])]});}
            var Q19;
            {var subQ0=sQuery(id+"F0.wireOp",EDGE,"E14");var subQ5=sQuery(id+"F0.wireOp",EDGE,"E11.MirrorCS");var subQ6=makeQuery(id+"F0.imprint","INTERSECT",VERTEX,{"derivedFrom":[subQ5,subQ0]});Q19=makeQuery(id+"F0.imprint","IMPRINT",FACE,{"disambiguationData":[TD([[makeQuery(id+"F0.imprint","IMPRINT",EDGE,{"disambiguationData":[TD([[subQ6,-1.0]])],"derivedFrom":subQ5}),1.0]])]});}
            var Q20;
            {var subQ0=sQuery(id+"F0.wireOp",EDGE,"E22.MirrorCS");var subQ1=sQuery(id+"F0.wireOp",EDGE,"E11.MirrorCS");var subQ2=makeQuery(id+"F0.imprint","INTERSECT",VERTEX,{"derivedFrom":[subQ1,subQ0]});Q20=makeQuery(id+"F0.imprint","IMPRINT",FACE,{"disambiguationData":[TD([[makeQuery(id+"F0.imprint","IMPRINT",EDGE,{"disambiguationData":[TD([[subQ2,-1.0]])],"derivedFrom":subQ1}),-1.0]])]});}
            var Q21;
            {var subQ0=sQuery(id+"F0.wireOp",EDGE,"E23.MirrorCS");var subQ1=sQuery(id+"F0.wireOp",EDGE,"E0.left");var subQ2=makeQuery(id+"F0.imprint","INTERSECT",VERTEX,{"derivedFrom":[subQ1,subQ0]});Q21=makeQuery(id+"F0.imprint","IMPRINT",FACE,{"disambiguationData":[TD([[makeQuery(id+"F0.imprint","IMPRINT",EDGE,{"disambiguationData":[TD([[subQ2,1.0]])],"derivedFrom":subQ1}),1.0]])]});}
            var Q22;
            {var subQ0=sQuery(id+"F0.wireOp",EDGE,"E24.MirrorCS");var subQ1=sQuery(id+"F0.wireOp",EDGE,"E13.MirrorCS");var subQ2=makeQuery(id+"F0.imprint","INTERSECT",VERTEX,{"derivedFrom":[subQ1,subQ0]});Q22=makeQuery(id+"F0.imprint","IMPRINT",FACE,{"disambiguationData":[TD([[makeQuery(id+"F0.imprint","IMPRINT",EDGE,{"disambiguationData":[TD([[subQ2,-1.0]])],"derivedFrom":subQ1}),1.0]])]});}
            var Q23;
            {var subQ0=sQuery(id+"F0.wireOp",EDGE,"E24.MirrorCS");var subQ1=sQuery(id+"F0.wireOp",EDGE,"E3");var subQ2=makeQuery(id+"F0.imprint","INTERSECT",VERTEX,{"derivedFrom":[subQ1,subQ0]});Q23=makeQuery(id+"F0.imprint","IMPRINT",FACE,{"disambiguationData":[TD([[makeQuery(id+"F0.imprint","IMPRINT",EDGE,{"disambiguationData":[TD([[subQ2,-1.0]])],"derivedFrom":subQ1}),1.0]])]});}
            var Q24;
            {var subQ0=sQuery(id+"F0.wireOp",EDGE,"E23.MirrorCS");var subQ1=sQuery(id+"F0.wireOp",EDGE,"E4");var subQ2=makeQuery(id+"F0.imprint","INTERSECT",VERTEX,{"derivedFrom":[subQ1,subQ0]});Q24=makeQuery(id+"F0.imprint","IMPRINT",FACE,{"disambiguationData":[TD([[makeQuery(id+"F0.imprint","IMPRINT",EDGE,{"disambiguationData":[TD([[subQ2,-1.0]])],"derivedFrom":subQ1}),-1.0]])]});}
            var Q25;
            {var subQ0=sQuery(id+"F0.wireOp",EDGE,"E23.MirrorCS");var subQ1=sQuery(id+"F0.wireOp",EDGE,"E3");var subQ2=makeQuery(id+"F0.imprint","INTERSECT",VERTEX,{"derivedFrom":[subQ1,subQ0]});Q25=makeQuery(id+"F0.imprint","IMPRINT",FACE,{"disambiguationData":[TD([[makeQuery(id+"F0.imprint","IMPRINT",EDGE,{"disambiguationData":[TD([[subQ2,-1.0]])],"derivedFrom":subQ1}),-1.0]])]});}
            var Q26;
            {var subQ0=sQuery(id+"F0.wireOp",EDGE,"E22.MirrorCS");var subQ1=sQuery(id+"F0.wireOp",EDGE,"E3");var subQ2=makeQuery(id+"F0.imprint","INTERSECT",VERTEX,{"derivedFrom":[subQ1,subQ0]});Q26=makeQuery(id+"F0.imprint","IMPRINT",FACE,{"disambiguationData":[TD([[makeQuery(id+"F0.imprint","IMPRINT",EDGE,{"disambiguationData":[TD([[subQ2,-1.0]])],"derivedFrom":subQ1}),1.0]])]});}
            var Q27;
            {var subQ0=sQuery(id+"F0.wireOp",EDGE,"E14");var subQ1=sQuery(id+"F0.wireOp",EDGE,"E4");var subQ2=makeQuery(id+"F0.imprint","INTERSECT",VERTEX,{"derivedFrom":[subQ1,subQ0]});Q27=makeQuery(id+"F0.imprint","IMPRINT",FACE,{"disambiguationData":[TD([[makeQuery(id+"F0.imprint","IMPRINT",EDGE,{"disambiguationData":[TD([[subQ2,-1.0]])],"derivedFrom":subQ1}),-1.0]])]});}
            var Q28;
            {var subQ0=sQuery(id+"F0.wireOp",EDGE,"E20");var subQ1=sQuery(id+"F0.wireOp",EDGE,"E3");var subQ2=makeQuery(id+"F0.imprint","INTERSECT",VERTEX,{"derivedFrom":[subQ1,subQ0]});Q28=makeQuery(id+"F0.imprint","IMPRINT",FACE,{"disambiguationData":[TD([[makeQuery(id+"F0.imprint","IMPRINT",EDGE,{"disambiguationData":[TD([[subQ2,-1.0]])],"derivedFrom":subQ1}),1.0]])]});}
            var Q29;
            {var subQ0=sQuery(id+"F0.wireOp",EDGE,"E22.MirrorCS");var subQ1=sQuery(id+"F0.wireOp",EDGE,"E13.MirrorCS");var subQ2=makeQuery(id+"F0.imprint","INTERSECT",VERTEX,{"derivedFrom":[subQ1,subQ0]});Q29=makeQuery(id+"F0.imprint","IMPRINT",FACE,{"disambiguationData":[TD([[makeQuery(id+"F0.imprint","IMPRINT",EDGE,{"disambiguationData":[TD([[subQ2,-1.0]])],"derivedFrom":subQ1}),1.0]])]});}
            var Q30;
            {var subQ0=sQuery(id+"F0.wireOp",EDGE,"E20");var subQ1=sQuery(id+"F0.wireOp",EDGE,"E13.MirrorCS");var subQ2=makeQuery(id+"F0.imprint","INTERSECT",VERTEX,{"derivedFrom":[subQ1,subQ0]});Q30=makeQuery(id+"F0.imprint","IMPRINT",FACE,{"disambiguationData":[TD([[makeQuery(id+"F0.imprint","IMPRINT",EDGE,{"disambiguationData":[TD([[subQ2,-1.0]])],"derivedFrom":subQ1}),1.0]])]});}
            var Q31;
            {var subQ0=sQuery(id+"F0.wireOp",EDGE,"E14");var subQ1=sQuery(id+"F0.wireOp",EDGE,"E3");var subQ2=makeQuery(id+"F0.imprint","INTERSECT",VERTEX,{"derivedFrom":[subQ1,subQ0]});Q31=makeQuery(id+"F0.imprint","IMPRINT",FACE,{"disambiguationData":[TD([[makeQuery(id+"F0.imprint","IMPRINT",EDGE,{"disambiguationData":[TD([[subQ2,-1.0]])],"derivedFrom":subQ1}),-1.0]])]});}
            var Q32;
            {var subQ0=sQuery(id+"F0.wireOp",EDGE,"E14");var subQ5=sQuery(id+"F0.wireOp",EDGE,"E11.MirrorCS");var subQ6=makeQuery(id+"F0.imprint","INTERSECT",VERTEX,{"derivedFrom":[subQ5,subQ0]});Q32=makeQuery(id+"F0.imprint","IMPRINT",FACE,{"disambiguationData":[TD([[makeQuery(id+"F0.imprint","IMPRINT",EDGE,{"disambiguationData":[TD([[subQ6,-1.0]])],"derivedFrom":subQ5}),1.0]])]});}
            extrude(context, id + "F3", {"entities" : qUnion([Q0, Q1, Q2, Q3, Q4, Q5, Q6, Q7, Q8, Q9, Q10, Q11, Q12, Q13, Q14, Q15, Q16, Q17, Q18, Q19, Q20, Q21, Q22, Q23, Q24, Q25, Q26, Q27, Q28, Q29, Q30, Q31, Q32]), "depth" : 30.48 * mm});
        }
        {
            var Q0;
            Q0=makeQuery(id+"F1.opExtrude","SWEPT_FACE",FACE,{"disambiguationData":[OSD([sQuery(id+"F0.wireOp",EDGE,"E25.7"),sQuery(id+"F0.wireOp",EDGE,"E25.8"),sQuery(id+"F0.wireOp",EDGE,"E25.9")])]});
            var sketch = newSketch(context, id + "F4", { "sketchPlane" : qUnion([Q0])});
            skLineSegment(sketch, "E26", {"start": v(-205.42, 25.4) * mm, "end": v(-228.6, 12.7) * mm});
            skLineSegment(sketch, "E27.MirrorCS", {"start": v(205.42, 25.4) * mm, "end": v(228.6, 12.7) * mm});
            skSolve(sketch);
        }
        {
            var Q0;
            {var subQ0=sQuery(id+"F4.wireOp",EDGE,"E26");Q0=makeQuery(id+"F4.imprint","IMPRINT",FACE,{"disambiguationData":[TD([[makeQuery(id+"F4.imprint","IMPRINT",EDGE,{"derivedFrom":subQ0}),-1.0]])]});}
            var Q1;
            {var subQ0=sQuery(id+"F4.wireOp",EDGE,"E27.MirrorCS");Q1=makeQuery(id+"F4.imprint","IMPRINT",FACE,{"disambiguationData":[TD([[makeQuery(id+"F4.imprint","IMPRINT",EDGE,{"derivedFrom":subQ0}),1.0]])]});}
            extrude(context, id + "F5", {"entities" : qUnion([Q0, Q1]), "operationType" : NewBodyOperationType.REMOVE, "oppositeDirection" : true, "depth" : 457.2 * mm});
        }
        {
            var Q0;
            Q0=qCreatedBy(makeId("Front.planeOp"),FACE);
            cPlane(context, id + "F6", {"entities" : qUnion([Q0]), "cplaneType" : CPlaneType.OFFSET, "offset" : 127 * mm, "oppositeDirection" : true, "width" : 152.4 * mm, "height" : 152.4 * mm});
        }
        {
            var Q0;
            Q0=qCreatedBy(id+"F6.planeOp",FACE);
            var sketch = newSketch(context, id + "F7", { "sketchPlane" : qUnion([Q0])});
            skCircle(sketch, "E28.cCircle", {"center": v(0, 0) * mm, "radius": 80.25 * mm, "construction": true});
            skLineSegment(sketch, "E28.0", {"start": v(-29.21, -80.25) * mm, "end": v(-73.96, -42.7) * mm});
            skLineSegment(sketch, "E28.1", {"start": v(-73.96, -42.7) * mm, "end": v(-84.1, 14.83) * mm});
            skLineSegment(sketch, "E28.2", {"start": v(-84.1, 14.83) * mm, "end": v(-54.9, 65.43) * mm});
            skLineSegment(sketch, "E28.3", {"start": v(-54.9, 65.43) * mm, "end": v(0, 85.4) * mm});
            skLineSegment(sketch, "E28.4", {"start": v(0, 85.4) * mm, "end": v(54.9, 65.42) * mm});
            skLineSegment(sketch, "E28.5", {"start": v(54.9, 65.42) * mm, "end": v(84.1, 14.83) * mm});
            skLineSegment(sketch, "E28.6", {"start": v(84.1, 14.83) * mm, "end": v(73.96, -42.7) * mm});
            skLineSegment(sketch, "E28.7", {"start": v(73.96, -42.7) * mm, "end": v(29.2, -80.26) * mm});
            skLineSegment(sketch, "E28.8", {"start": v(29.2, -80.26) * mm, "end": v(-29.21, -80.25) * mm});
            skPoint(sketch, "E28.0.midPoint", {"position": v(-51.59, -61.47) * mm});
            skSolve(sketch);
        }
        {
            var Q0;
            Q0=qCreatedBy(makeId("Front.planeOp"),FACE);
            var sketch = newSketch(context, id + "F8", { "sketchPlane" : qUnion([Q0])});
            skCircle(sketch, "E29.cCircle", {"center": v(0, 0) * mm, "radius": 35.78 * mm, "construction": true});
            skLineSegment(sketch, "E29.0", {"start": v(34.74, -22.37) * mm, "end": v(-2, -41.27) * mm});
            skLineSegment(sketch, "E29.1", {"start": v(-2, -41.27) * mm, "end": v(-36.74, -18.9) * mm});
            skLineSegment(sketch, "E29.2", {"start": v(-36.74, -18.9) * mm, "end": v(-34.74, 22.37) * mm});
            skLineSegment(sketch, "E29.3", {"start": v(-34.74, 22.37) * mm, "end": v(2, 41.27) * mm});
            skLineSegment(sketch, "E29.4", {"start": v(2, 41.27) * mm, "end": v(36.74, 18.9) * mm});
            skLineSegment(sketch, "E29.5", {"start": v(36.74, 18.9) * mm, "end": v(34.74, -22.37) * mm});
            skPoint(sketch, "E29.0.midPoint", {"position": v(16.37, -31.82) * mm});
            skSolve(sketch);
        }
        {
            var Q0;
            Q0=makeQuery(id+"F7.imprint","IMPRINT",FACE,{"disambiguationData":[TD([[makeQuery(id+"F7.imprint","IMPRINT",EDGE,{"derivedFrom":sQuery(id+"F7.wireOp",EDGE,"E28.0")}),-1.0]])]});
            var Q1;
            Q1 = qSketchRegion(id + "F8", true);
            loft(context, id + "F9", {"sheetProfilesArray" : [{ "sheetProfileEntities" : qUnion([Q0]) }, { "sheetProfileEntities" : qUnion([Q1]) }]});
        }
    });
